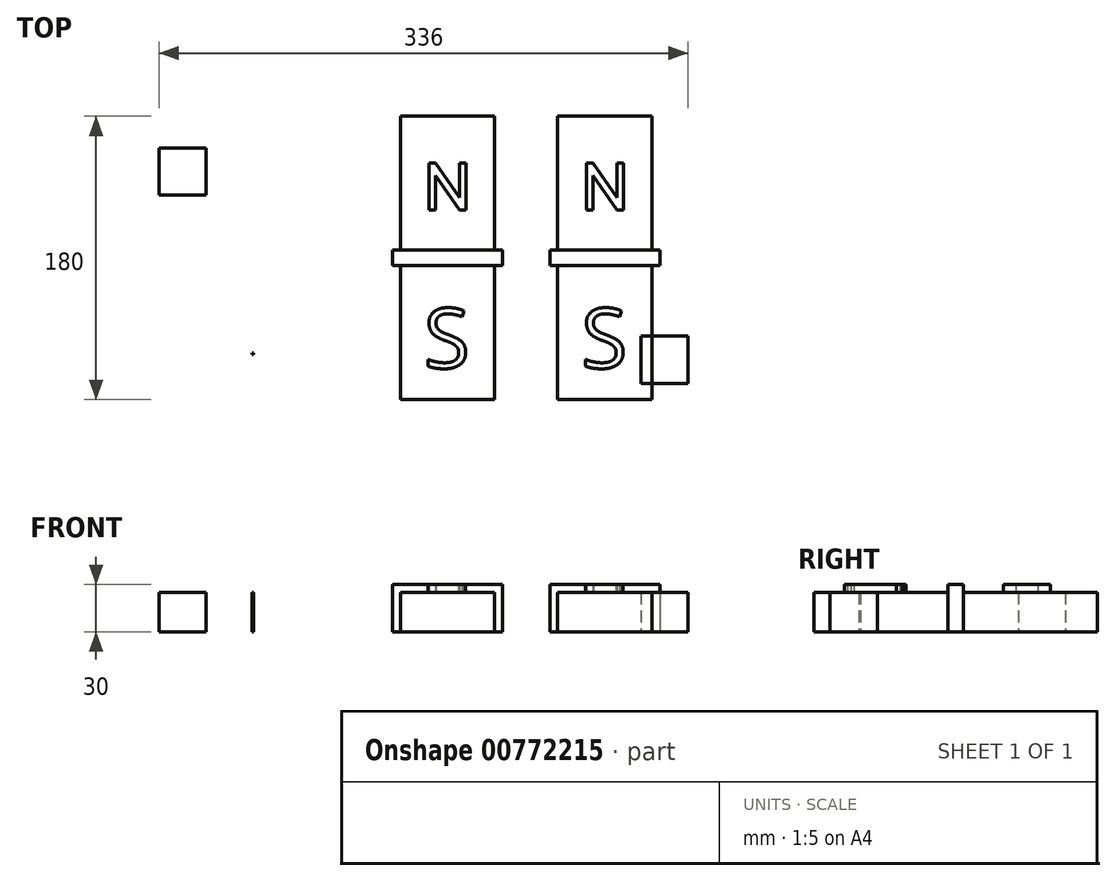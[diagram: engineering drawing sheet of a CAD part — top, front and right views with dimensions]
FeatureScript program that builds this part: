
annotation { "Feature Type Name" : "Feature", "Feature Type Description" : "" }
export const myFeature = defineFeature(function(context is Context, id is Id, definition is map)
    precondition{}
    {
        {
            var Q0;
            Q0=qCreatedBy(makeId("Top.planeOp"),FACE);
            var sketch = newSketch(context, id + "F0", { "sketchPlane" : qUnion([Q0])});
            skLineSegment(sketch, "E0.bottom", {"start": v(-35.03, 89.52) * mm, "end": v(24.97, 89.52) * mm});
            skLineSegment(sketch, "E0.top", {"start": v(-35.03, -90.48) * mm, "end": v(24.97, -90.48) * mm});
            skLineSegment(sketch, "E0.left", {"start": v(-35.03, 89.52) * mm, "end": v(-35.03, -90.48) * mm});
            skLineSegment(sketch, "E0.right", {"start": v(24.97, 89.52) * mm, "end": v(24.97, -90.48) * mm});
            skSolve(sketch);
        }
        {
            var Q0;
            Q0 = qSketchRegion(id + "F0", true);
            extrude(context, id + "F1", {"entities" : qUnion([Q0]), "depth" : 25 * mm, "offsetDistance" : 25 * mm});
        }
        {
            var Q0;
            Q0=qCreatedBy(makeId("Top.planeOp"),FACE);
            var sketch = newSketch(context, id + "F2", { "sketchPlane" : qUnion([Q0])});
            skLineSegment(sketch, "E1.bottom", {"start": v(-129.1, -60.95) * mm, "end": v(-128.1, -60.95) * mm});
            skLineSegment(sketch, "E1.top", {"start": v(-129.1, -61.95) * mm, "end": v(-128.1, -61.95) * mm});
            skLineSegment(sketch, "E1.left", {"start": v(-129.1, -60.95) * mm, "end": v(-129.1, -61.95) * mm});
            skLineSegment(sketch, "E1.right", {"start": v(-128.1, -60.95) * mm, "end": v(-128.1, -61.95) * mm});
            skSolve(sketch);
        }
        {
            var Q0;
            Q0 = qSketchRegion(id + "F2", true);
            extrude(context, id + "F3", {"entities" : qUnion([Q0]), "depth" : 25 * mm, "offsetDistance" : 25 * mm});
        }
        {
            var Q0;
            Q0=qCreatedBy(makeId("Top.planeOp"),FACE);
            var sketch = newSketch(context, id + "F4", { "sketchPlane" : qUnion([Q0])});
            skLineSegment(sketch, "E2.bottom", {"start": v(-188.28, 69.26) * mm, "end": v(-158.28, 69.26) * mm});
            skLineSegment(sketch, "E2.top", {"start": v(-188.28, 39.26) * mm, "end": v(-158.28, 39.26) * mm});
            skLineSegment(sketch, "E2.left", {"start": v(-188.28, 69.26) * mm, "end": v(-188.28, 39.26) * mm});
            skLineSegment(sketch, "E2.right", {"start": v(-158.28, 69.26) * mm, "end": v(-158.28, 39.26) * mm});
            skLineSegment(sketch, "E3.bottom", {"start": v(147.72, -80.24) * mm, "end": v(117.72, -80.24) * mm});
            skLineSegment(sketch, "E3.top", {"start": v(147.72, -50.24) * mm, "end": v(117.72, -50.24) * mm});
            skLineSegment(sketch, "E3.left", {"start": v(147.72, -80.24) * mm, "end": v(147.72, -50.24) * mm});
            skLineSegment(sketch, "E3.right", {"start": v(117.72, -80.24) * mm, "end": v(117.72, -50.24) * mm});
            skSolve(sketch);
        }
        {
            var Q0;
            Q0 = qSketchRegion(id + "F4", true);
            extrude(context, id + "F5", {"entities" : qUnion([Q0]), "depth" : 25 * mm, "offsetDistance" : 25 * mm});
        }
        {
            var Q0;
            Q0=makeQuery(id+"F1.opExtrude","CAP_FACE",FACE,{"disambiguationData":[OSD([sQuery(id+"F0.wireOp",EDGE,"E0.bottom"),sQuery(id+"F0.wireOp",EDGE,"E0.top"),sQuery(id+"F0.wireOp",EDGE,"E0.left"),sQuery(id+"F0.wireOp",EDGE,"E0.right")])],"isStart":false});
            var sketch = newSketch(context, id + "F6", { "sketchPlane" : qUnion([Q0])});
            skLineSegment(sketch, "E4", {"start": v(-16.73, 29.76) * mm, "end": v(-16.73, 59.76) * mm});
            skLineSegment(sketch, "E5", {"start": v(-16.73, 59.76) * mm, "end": v(-12.73, 59.76) * mm});
            skLineSegment(sketch, "E6", {"start": v(-12.73, 59.76) * mm, "end": v(2.68, 37.76) * mm});
            skLineSegment(sketch, "E7", {"start": v(2.68, 37.76) * mm, "end": v(2.68, 59.76) * mm});
            skLineSegment(sketch, "E8", {"start": v(2.68, 59.76) * mm, "end": v(6.68, 59.76) * mm});
            skLineSegment(sketch, "E9", {"start": v(6.68, 59.76) * mm, "end": v(6.68, 29.76) * mm});
            skLineSegment(sketch, "E10", {"start": v(-12.73, 51.76) * mm, "end": v(-12.73, 29.76) * mm});
            skLineSegment(sketch, "E11", {"start": v(6.68, 29.76) * mm, "end": v(2.68, 29.76) * mm});
            skLineSegment(sketch, "E12", {"start": v(2.68, 29.76) * mm, "end": v(-12.73, 51.76) * mm});
            skLineSegment(sketch, "E13", {"start": v(-16.73, 29.76) * mm, "end": v(-12.73, 29.76) * mm});
            skLineSegment(sketch, "E14", {"start": v(-5.03, 40.76) * mm, "end": v(-5.03, 0) * mm});
            skLineSegment(sketch, "E15", {"start": v(-5.03, 48.76) * mm, "end": v(-5.03, 89.52) * mm});
            skLineSegment(sketch, "E16", {"start": v(-16.73, 44.76) * mm, "end": v(-35.03, 44.76) * mm});
            skLineSegment(sketch, "E17", {"start": v(6.68, 44.76) * mm, "end": v(24.97, 44.76) * mm});
            skSolve(sketch);
        }
        {
            var Q0;
            Q0 = qSketchRegion(id + "F6", true);
            extrude(context, id + "F7", {"entities" : qUnion([Q0]), "operationType" : NewBodyOperationType.ADD, "depth" : 5 * mm, "offsetDistance" : 25 * mm});
        }
        {
            var Q0;
            Q0=makeQuery(id+"F1.opExtrude","CAP_FACE",FACE,{"disambiguationData":[OSD([sQuery(id+"F0.wireOp",EDGE,"E0.bottom"),sQuery(id+"F0.wireOp",EDGE,"E0.top"),sQuery(id+"F0.wireOp",EDGE,"E0.left"),sQuery(id+"F0.wireOp",EDGE,"E0.right")])],"isStart":false});
            var sketch = newSketch(context, id + "F8", { "sketchPlane" : qUnion([Q0])});
            skText(sketch, "E18", { "text": "S", "fontName": "OpenSans-Regular.ttf"});
            const initialGuessF8  = {"E18": [-0.02003, -0.07048, 1, 0, 0.03818]};
            skSetInitialGuess(sketch, initialGuessF8);
            skSolve(sketch);
        }
        {
            var Q0;
            Q0 = qSketchRegion(id + "F8", true);
            extrude(context, id + "F9", {"entities" : qUnion([Q0]), "operationType" : NewBodyOperationType.ADD, "depth" : 5 * mm, "offsetDistance" : 25 * mm});
        }
        {
            var Q0;
            Q0=makeQuery(id+"F1.opExtrude","CAP_FACE",FACE,{"disambiguationData":[OSD([sQuery(id+"F0.wireOp",EDGE,"E0.bottom"),sQuery(id+"F0.wireOp",EDGE,"E0.top"),sQuery(id+"F0.wireOp",EDGE,"E0.left"),sQuery(id+"F0.wireOp",EDGE,"E0.right")])],"isStart":false});
            var sketch = newSketch(context, id + "F10", { "sketchPlane" : qUnion([Q0])});
            skLineSegment(sketch, "E19", {"start": v(24.97, -0.48) * mm, "end": v(-35.03, 0) * mm});
            skLineSegment(sketch, "E20.bottom", {"start": v(-35.03, 4.52) * mm, "end": v(24.97, 4.52) * mm});
            skLineSegment(sketch, "E20.top", {"start": v(-35.03, -5.48) * mm, "end": v(24.97, -5.48) * mm});
            skLineSegment(sketch, "E20.left", {"start": v(-35.03, 4.52) * mm, "end": v(-35.03, -5.48) * mm});
            skLineSegment(sketch, "E20.right", {"start": v(24.97, 4.52) * mm, "end": v(24.97, -5.48) * mm});
            skLineSegment(sketch, "E21", {"start": v(-5.03, -5.48) * mm, "end": v(-4.8, -90.48) * mm});
            skLineSegment(sketch, "E22", {"start": v(-5.03, 4.52) * mm, "end": v(-5.03, 89.52) * mm});
            skLineSegment(sketch, "E23.bottom", {"start": v(-35.03, -5.48) * mm, "end": v(-40.03, -5.48) * mm});
            skLineSegment(sketch, "E23.top", {"start": v(-35.03, 4.52) * mm, "end": v(-40.03, 4.52) * mm});
            skLineSegment(sketch, "E23.left", {"start": v(-35.03, -5.48) * mm, "end": v(-35.03, 4.52) * mm});
            skLineSegment(sketch, "E23.right", {"start": v(-40.03, -5.48) * mm, "end": v(-40.03, 4.52) * mm});
            skLineSegment(sketch, "E24.bottom", {"start": v(24.97, 4.52) * mm, "end": v(29.97, 4.52) * mm});
            skLineSegment(sketch, "E24.top", {"start": v(24.97, -5.48) * mm, "end": v(29.97, -5.48) * mm});
            skLineSegment(sketch, "E24.right", {"start": v(29.97, 4.52) * mm, "end": v(29.97, -5.48) * mm});
            skSolve(sketch);
        }
        {
            var Q0;
            Q0 = qSketchRegion(id + "F10", true);
            extrude(context, id + "F11", {"entities" : qUnion([Q0]), "operationType" : NewBodyOperationType.ADD, "depth" : 5 * mm, "offsetDistance" : 25 * mm, "hasSecondDirection" : true, "secondDirectionOppositeDirection" : true, "secondDirectionDepth" : 25 * mm});
        }
        {
            var Q0;
            Q0=makeQuery(id+"F1.opExtrude","SWEPT_BODY",BODY,{"disambiguationData":[OSD([sQuery(id+"F0.wireOp",EDGE,"E0.bottom"),sQuery(id+"F0.wireOp",EDGE,"E0.top"),sQuery(id+"F0.wireOp",EDGE,"E0.left"),sQuery(id+"F0.wireOp",EDGE,"E0.right")])]});
            transform(context, id + "F12", {"entities" : qUnion([Q0]), "transformType" : TransformType.TRANSLATION_3D, "dx" : 100 * mm, "dy" : 0 * mm, "dz" : 0 * mm, "makeCopy" : true});
        }
    });
